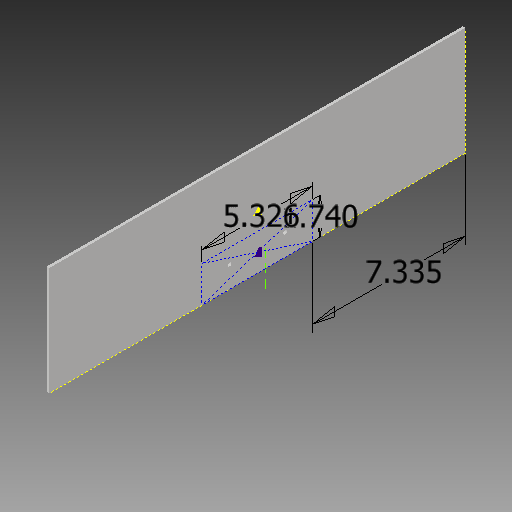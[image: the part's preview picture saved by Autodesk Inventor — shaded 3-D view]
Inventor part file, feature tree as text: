
AUTODESK INVENTOR PART (.ipt)
format: ipt  version: 2017 (Build 210142000, 142)  size: 110,592 bytes
history: native  units: in
note: dims shown in document units (in); Inventor stores cm internally (conversion verified against a paired STEP export)
features: sketch x3, extrude x1, hole x1
ambient origin geometry x8: Origin, YZ Plane, XZ Plane, XY Plane, X Axis, Y Axis, Z Axis, Center Point
bodies: Solid1 (feature_tree)
feature tree (5):
  extrude  "Extrusion1"  Depth=5.22in
  sketch  "Sketch2"  dims[d2=0.125in d3=0.0in d4=5.326in]
  hole  "Hole1"  [1 undecoded]
  sketch  "Sketch1"  dims[d0=20.0in d1=5.22in]
  sketch  "Sketch3"  dims[d5=1.74in d6=7.335in d7=1.035in d10=0.177in d11=0.75in d12=0.409in d13=0.25in d14=90.0deg d15=1.0in d16=0.8108in d17=1.332in d18=1.332in]
note: 1 required parameter value undecoded (feature->parameter linkage not recoverable at this tier; creation-order binding heuristic only, values carry confidence <= 0.55)
